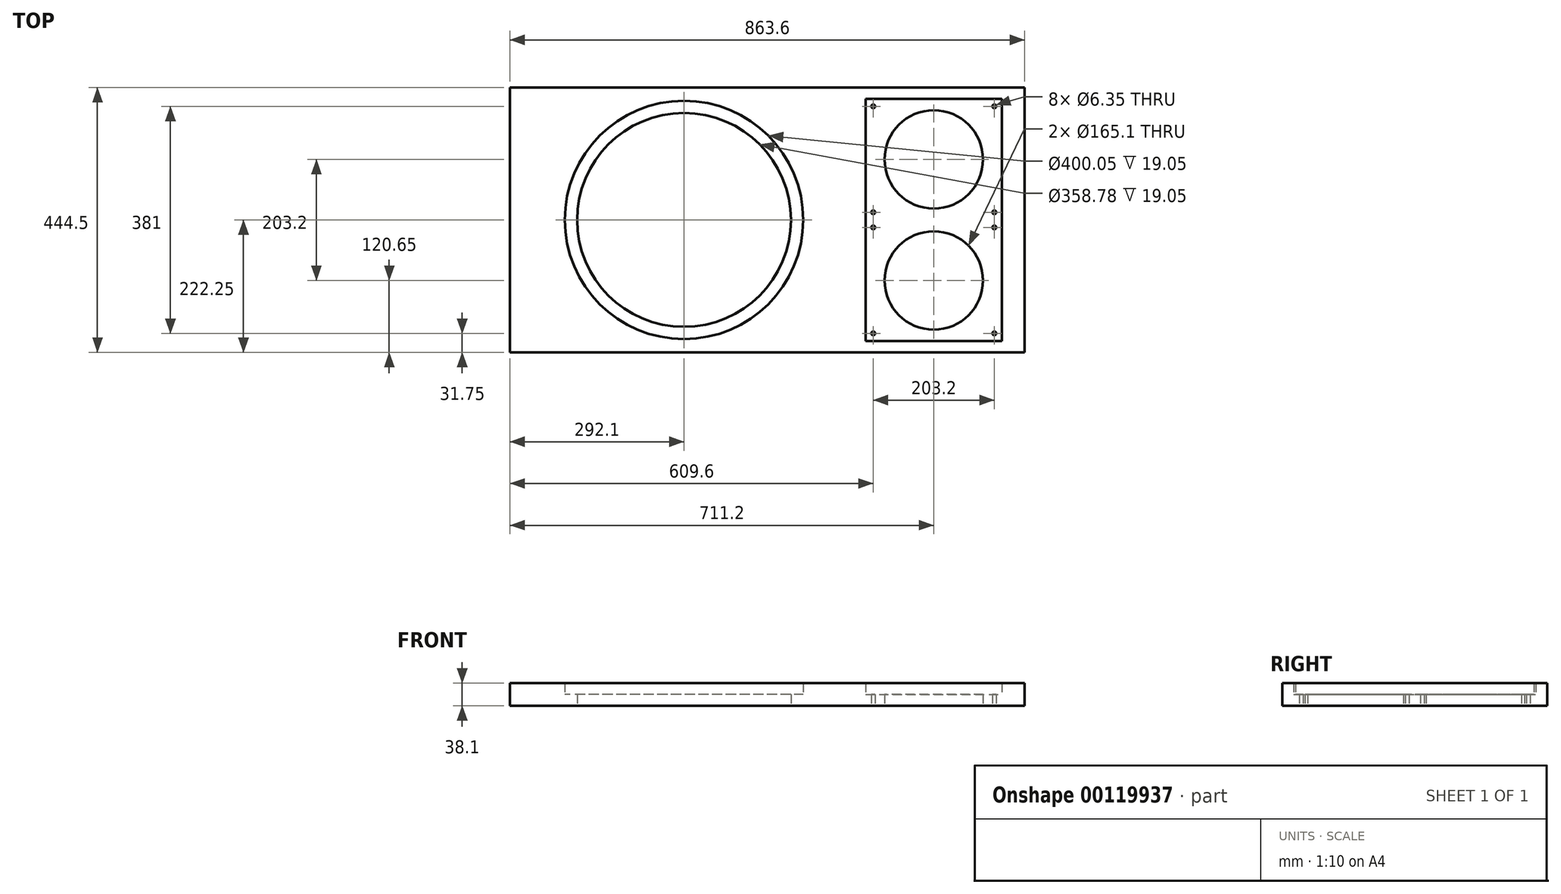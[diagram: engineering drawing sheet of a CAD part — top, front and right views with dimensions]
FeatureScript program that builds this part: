
annotation { "Feature Type Name" : "Feature", "Feature Type Description" : "" }
export const myFeature = defineFeature(function(context is Context, id is Id, definition is map)
    precondition{}
    {
        {
            var Q0;
            Q0=qCreatedBy(makeId("Top.planeOp"),FACE);
            var sketch = newSketch(context, id + "F0", { "sketchPlane" : qUnion([Q0])});
            skLineSegment(sketch, "E0.bottom", {"start": v(0, 0) * mm, "end": v(863.6, 0) * mm});
            skLineSegment(sketch, "E0.top", {"start": v(0, 444.5) * mm, "end": v(863.6, 444.5) * mm});
            skLineSegment(sketch, "E0.left", {"start": v(0, 0) * mm, "end": v(0, 444.5) * mm});
            skLineSegment(sketch, "E0.right", {"start": v(863.6, 0) * mm, "end": v(863.6, 444.5) * mm});
            skLineSegment(sketch, "E1.bottom", {"start": v(596.9, 19.05) * mm, "end": v(825.5, 19.05) * mm});
            skLineSegment(sketch, "E1.top", {"start": v(596.9, 425.45) * mm, "end": v(825.5, 425.45) * mm});
            skLineSegment(sketch, "E1.left", {"start": v(596.9, 19.05) * mm, "end": v(596.9, 425.45) * mm});
            skLineSegment(sketch, "E1.right", {"start": v(825.5, 19.05) * mm, "end": v(825.5, 425.45) * mm});
            skCircle(sketch, "E2", {"center": v(711.2, 323.85) * mm, "radius": 82.55 * mm});
            skCircle(sketch, "E3", {"center": v(711.2, 120.65) * mm, "radius": 82.55 * mm});
            skCircle(sketch, "E4", {"center": v(292.1, 222.25) * mm, "radius": 179.39 * mm});
            skCircle(sketch, "E5", {"center": v(292.1, 222.25) * mm, "radius": 200.03 * mm});
            skCircle(sketch, "E6", {"center": v(609.6, 412.75) * mm, "radius": 3.18 * mm});
            skCircle(sketch, "E7", {"center": v(812.8, 412.75) * mm, "radius": 3.18 * mm});
            skCircle(sketch, "E8", {"center": v(609.6, 234.95) * mm, "radius": 3.18 * mm});
            skCircle(sketch, "E9", {"center": v(609.6, 209.55) * mm, "radius": 3.18 * mm});
            skCircle(sketch, "E10", {"center": v(609.6, 31.75) * mm, "radius": 3.18 * mm});
            skCircle(sketch, "E11", {"center": v(812.8, 31.75) * mm, "radius": 3.18 * mm});
            skCircle(sketch, "E12", {"center": v(812.8, 234.95) * mm, "radius": 3.18 * mm});
            skCircle(sketch, "E13", {"center": v(812.8, 209.55) * mm, "radius": 3.18 * mm});
            skSolve(sketch);
        }
        {
            var Q0;
            Q0=makeQuery(id+"F0.imprint","IMPRINT",FACE,{"disambiguationData":[TD([[makeQuery(id+"F0.imprint","IMPRINT",EDGE,{"derivedFrom":sQuery(id+"F0.wireOp",EDGE,"E0.bottom")}),1.0]])]});
            extrude(context, id + "F1", {"entities" : qUnion([Q0]), "depth" : 38.1 * mm});
        }
        {
            var Q0;
            Q0=makeQuery(id+"F0.imprint","IMPRINT",FACE,{"disambiguationData":[TD([[makeQuery(id+"F0.imprint","IMPRINT",EDGE,{"derivedFrom":sQuery(id+"F0.wireOp",EDGE,"E4")}),-1.0]])]});
            var Q1;
            Q1=makeQuery(id+"F0.imprint","IMPRINT",FACE,{"disambiguationData":[TD([[makeQuery(id+"F0.imprint","IMPRINT",EDGE,{"derivedFrom":sQuery(id+"F0.wireOp",EDGE,"E1.bottom")}),1.0]])]});
            extrude(context, id + "F2", {"entities" : qUnion([Q0, Q1]), "operationType" : NewBodyOperationType.ADD, "depth" : 19.05 * mm});
        }
    });
